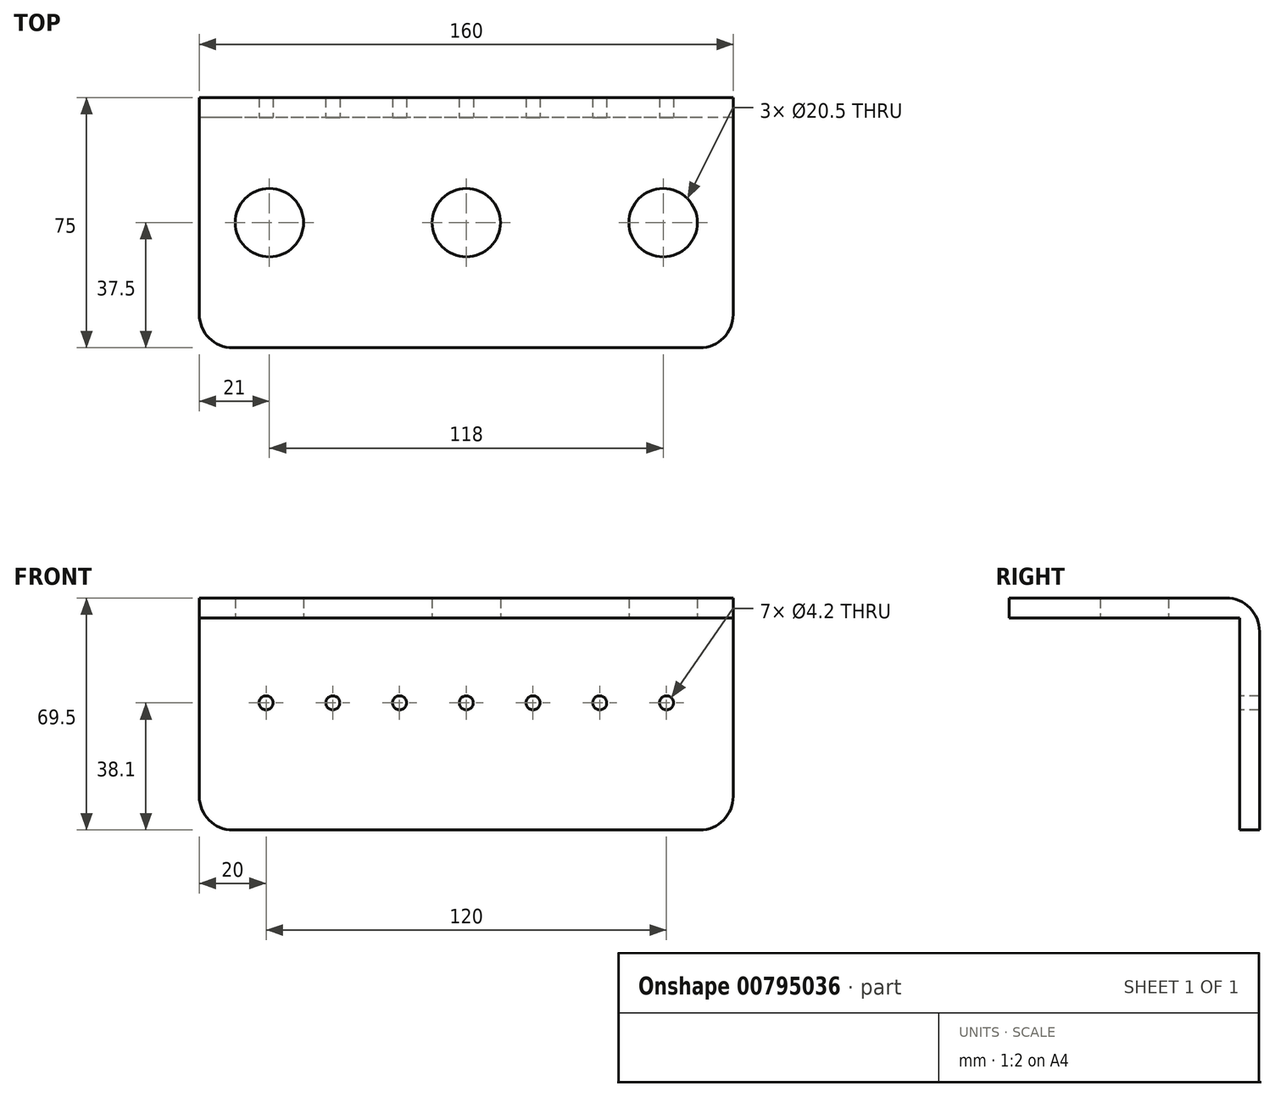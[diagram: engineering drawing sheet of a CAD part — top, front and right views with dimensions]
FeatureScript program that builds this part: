
annotation { "Feature Type Name" : "Feature", "Feature Type Description" : "" }
export const myFeature = defineFeature(function(context is Context, id is Id, definition is map)
    precondition{}
    {
        {
            var Q0;
            Q0=qCreatedBy(makeId("Top.planeOp"),FACE);
            var sketch = newSketch(context, id + "F0", { "sketchPlane" : qUnion([Q0])});
            skLineSegment(sketch, "E0.bottom", {"start": v(80, 37.5) * mm, "end": v(-80, 37.5) * mm});
            skLineSegment(sketch, "E0.top", {"start": v(80, -37.5) * mm, "end": v(-80, -37.5) * mm});
            skLineSegment(sketch, "E0.left", {"start": v(80, 37.5) * mm, "end": v(80, -37.5) * mm});
            skLineSegment(sketch, "E0.right", {"start": v(-80, 37.5) * mm, "end": v(-80, -37.5) * mm});
            skPoint(sketch, "E0.middle", {"position": v(0, 0) * mm});
            skCircle(sketch, "E1", {"center": v(-59, 0) * mm, "radius": 10.25 * mm});
            skCircle(sketch, "E2", {"center": v(0, 0) * mm, "radius": 10.25 * mm});
            skCircle(sketch, "E3", {"center": v(59, 0) * mm, "radius": 10.25 * mm});
            skSolve(sketch);
        }
        {
            var Q0;
            Q0 = qSketchRegion(id + "F0", true);
            extrude(context, id + "F1", {"entities" : qUnion([Q0]), "depth" : 6 * mm, "offsetDistance" : 25 * mm});
        }
        {
            var Q0;
            Q0=makeQuery(id+"F1.opExtrude","SWEPT_FACE",FACE,{"disambiguationData":[OSD([sQuery(id+"F0.wireOp",EDGE,"E0.bottom")])]});
            var sketch = newSketch(context, id + "F2", { "sketchPlane" : qUnion([Q0])});
            skLineSegment(sketch, "E4.bottom", {"start": v(-80, 0) * mm, "end": v(80, 0) * mm});
            skLineSegment(sketch, "E4.top", {"start": v(-80, -63.5) * mm, "end": v(80, -63.5) * mm});
            skLineSegment(sketch, "E4.left", {"start": v(-80, 0) * mm, "end": v(-80, -63.5) * mm});
            skLineSegment(sketch, "E4.right", {"start": v(80, 0) * mm, "end": v(80, -63.5) * mm});
            skSolve(sketch);
        }
        {
            var Q0;
            Q0 = qSketchRegion(id + "F2", true);
            extrude(context, id + "F3", {"entities" : qUnion([Q0]), "operationType" : NewBodyOperationType.ADD, "oppositeDirection" : true, "depth" : 6 * mm, "offsetDistance" : 25 * mm});
        }
        {
            var Q0;
            Q0=makeQuery(id+"F1.opExtrude","CAP_EDGE",EDGE,{"disambiguationData":[OSD([sQuery(id+"F0.wireOp",EDGE,"E0.bottom")])],"isStart":false});
            var Q1;
            Q1=makeQuery(id+"F3.opExtrude","SWEPT_EDGE",EDGE,{"disambiguationData":[OSD([sQuery(id+"F2.wireOp",EDGE,"E4.top"),sQuery(id+"F2.wireOp",EDGE,"E4.right")])]});
            var Q2;
            Q2=makeQuery(id+"F3.opExtrude","SWEPT_EDGE",EDGE,{"disambiguationData":[OSD([sQuery(id+"F2.wireOp",EDGE,"E4.top"),sQuery(id+"F2.wireOp",EDGE,"E4.left")])]});
            var Q3;
            Q3=makeQuery(id+"F1.opExtrude","SWEPT_EDGE",EDGE,{"disambiguationData":[OSD([sQuery(id+"F0.wireOp",EDGE,"E0.top"),sQuery(id+"F0.wireOp",EDGE,"E0.left")])]});
            var Q4;
            Q4=makeQuery(id+"F1.opExtrude","SWEPT_EDGE",EDGE,{"disambiguationData":[OSD([sQuery(id+"F0.wireOp",EDGE,"E0.top"),sQuery(id+"F0.wireOp",EDGE,"E0.right")])]});
            fillet(context, id + "F4", {"entities" : qUnion([Q0, Q1, Q2, Q3, Q4]), "radius" : 10 * mm, "tangentPropagation" : true, "allowEdgeOverflow" : false});
        }
        {
            var Q0;
            Q0=makeQuery(id+"F3.opExtrude","CAP_FACE",FACE,{"disambiguationData":[OSD([sQuery(id+"F2.wireOp",EDGE,"E4.bottom"),sQuery(id+"F2.wireOp",EDGE,"E4.top"),sQuery(id+"F2.wireOp",EDGE,"E4.left"),sQuery(id+"F2.wireOp",EDGE,"E4.right")])],"isStart":false});
            var sketch = newSketch(context, id + "F5", { "sketchPlane" : qUnion([Q0])});
            skCircle(sketch, "E5", {"center": v(-60, -25.4) * mm, "radius": 2.1 * mm});
            skCircle(sketch, "E6", {"center": v(-40, -25.4) * mm, "radius": 2.1 * mm});
            skCircle(sketch, "E7", {"center": v(-20, -25.4) * mm, "radius": 2.1 * mm});
            skCircle(sketch, "E8", {"center": v(0, -25.4) * mm, "radius": 2.1 * mm});
            skCircle(sketch, "E9", {"center": v(20, -25.4) * mm, "radius": 2.1 * mm});
            skCircle(sketch, "E10", {"center": v(40, -25.4) * mm, "radius": 2.1 * mm});
            skCircle(sketch, "E11", {"center": v(60, -25.4) * mm, "radius": 2.1 * mm});
            skSolve(sketch);
        }
        {
            var Q0;
            Q0 = qSketchRegion(id + "F5", true);
            extrude(context, id + "F6", {"entities" : qUnion([Q0]), "operationType" : NewBodyOperationType.REMOVE, "oppositeDirection" : true, "depth" : 25 * mm, "offsetDistance" : 25 * mm});
        }
    });
